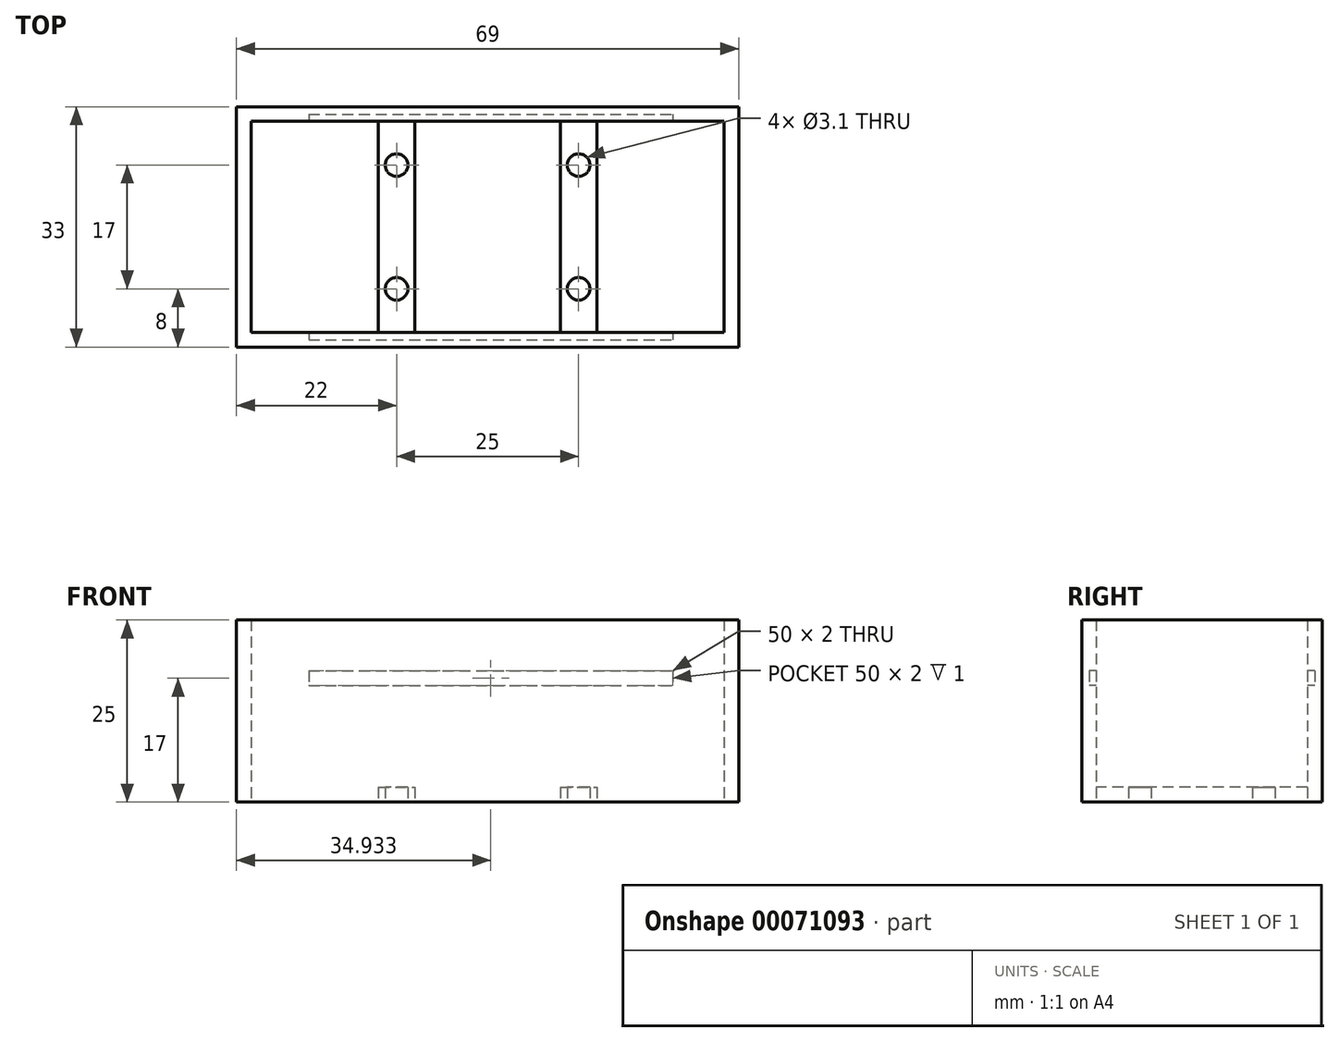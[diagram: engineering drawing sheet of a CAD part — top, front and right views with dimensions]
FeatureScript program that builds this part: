
annotation { "Feature Type Name" : "Feature", "Feature Type Description" : "" }
export const myFeature = defineFeature(function(context is Context, id is Id, definition is map)
    precondition{}
    {
        {
            var Q0;
            Q0=qCreatedBy(makeId("Top.planeOp"),FACE);
            var sketch = newSketch(context, id + "F0", { "sketchPlane" : qUnion([Q0])});
            skLineSegment(sketch, "E0.bottom", {"start": v(0, 0) * mm, "end": v(65, 0) * mm});
            skLineSegment(sketch, "E0.top", {"start": v(0, -29) * mm, "end": v(65, -29) * mm});
            skLineSegment(sketch, "E0.left", {"start": v(0, 0) * mm, "end": v(0, -29) * mm});
            skLineSegment(sketch, "E0.right", {"start": v(65, 0) * mm, "end": v(65, -29) * mm});
            skLineSegment(sketch, "E1.bottom", {"start": v(-2, 2) * mm, "end": v(67, 2) * mm});
            skLineSegment(sketch, "E1.top", {"start": v(-2, -31) * mm, "end": v(67, -31) * mm});
            skLineSegment(sketch, "E1.left", {"start": v(-2, 2) * mm, "end": v(-2, -31) * mm});
            skLineSegment(sketch, "E1.right", {"start": v(67, 2) * mm, "end": v(67, -31) * mm});
            skLineSegment(sketch, "E2.bottom", {"start": v(0, -29) * mm, "end": v(5, -29) * mm});
            skLineSegment(sketch, "E2.top", {"start": v(0, -24) * mm, "end": v(5, -24) * mm});
            skLineSegment(sketch, "E2.left", {"start": v(0, -29) * mm, "end": v(0, -24) * mm});
            skLineSegment(sketch, "E2.right", {"start": v(5, -29) * mm, "end": v(5, -24) * mm});
            skLineSegment(sketch, "E3.bottom", {"start": v(0, 0) * mm, "end": v(5, 0) * mm});
            skLineSegment(sketch, "E3.top", {"start": v(0, -5) * mm, "end": v(5, -5) * mm});
            skLineSegment(sketch, "E3.left", {"start": v(0, 0) * mm, "end": v(0, -5) * mm});
            skLineSegment(sketch, "E3.right", {"start": v(5, 0) * mm, "end": v(5, -5) * mm});
            skLineSegment(sketch, "E4.bottom", {"start": v(65, 0) * mm, "end": v(60, 0) * mm});
            skLineSegment(sketch, "E4.top", {"start": v(65, -5) * mm, "end": v(60, -5) * mm});
            skLineSegment(sketch, "E4.left", {"start": v(65, 0) * mm, "end": v(65, -5) * mm});
            skLineSegment(sketch, "E4.right", {"start": v(60, 0) * mm, "end": v(60, -5) * mm});
            skLineSegment(sketch, "E5.bottom", {"start": v(65, -29) * mm, "end": v(60, -29) * mm});
            skLineSegment(sketch, "E5.top", {"start": v(65, -24) * mm, "end": v(60, -24) * mm});
            skLineSegment(sketch, "E5.left", {"start": v(65, -29) * mm, "end": v(65, -24) * mm});
            skLineSegment(sketch, "E5.right", {"start": v(60, -29) * mm, "end": v(60, -24) * mm});
            skCircle(sketch, "E6", {"center": v(2.5, -2.5) * mm, "radius": 1.55 * mm});
            skCircle(sketch, "E7", {"center": v(2.5, -26.5) * mm, "radius": 1.55 * mm});
            skPoint(sketch, "E7.centerSnap0", {"position": v(2.5, -24) * mm});
            skPoint(sketch, "E7.centerSnap1", {"position": v(0, -26.5) * mm});
            skCircle(sketch, "E8", {"center": v(62.5, -26.5) * mm, "radius": 1.55 * mm});
            skPoint(sketch, "E8.centerSnap0", {"position": v(62.5, -24) * mm});
            skPoint(sketch, "E8.centerSnap1", {"position": v(5, -26.5) * mm});
            skCircle(sketch, "E9", {"center": v(62.5, -2.5) * mm, "radius": 1.55 * mm});
            skPoint(sketch, "E9.centerSnap0", {"position": v(60, -2.5) * mm});
            skPoint(sketch, "E9.centerSnap1", {"position": v(62.5, -5) * mm});
            skSolve(sketch);
        }
        {
            var Q0;
            Q0 = qSketchRegion(id + "F0", true);
            var Q1;
            Q1=makeQuery(id+"F0.imprint","IMPRINT",FACE,{"disambiguationData":[TD([[makeQuery(id+"F0.imprint","IMPRINT",EDGE,{"derivedFrom":sQuery(id+"F0.wireOp",EDGE,"E3.bottom")}),-1.0]])]});
            var Q2;
            Q2=makeQuery(id+"F0.imprint","IMPRINT",FACE,{"disambiguationData":[TD([[makeQuery(id+"F0.imprint","IMPRINT",EDGE,{"derivedFrom":sQuery(id+"F0.wireOp",EDGE,"E4.bottom")}),1.0]])]});
            var Q3;
            Q3=makeQuery(id+"F0.imprint","IMPRINT",FACE,{"disambiguationData":[TD([[makeQuery(id+"F0.imprint","IMPRINT",EDGE,{"derivedFrom":sQuery(id+"F0.wireOp",EDGE,"E5.bottom")}),-1.0]])]});
            var Q4;
            Q4=makeQuery(id+"F0.imprint","IMPRINT",FACE,{"disambiguationData":[TD([[makeQuery(id+"F0.imprint","IMPRINT",EDGE,{"derivedFrom":sQuery(id+"F0.wireOp",EDGE,"E2.bottom")}),1.0]])]});
            extrude(context, id + "F1", {"entities" : qUnion([Q0, Q1, Q2, Q3, Q4]), "depth" : 25 * mm});
        }
        {
            var Q0;
            Q0=makeQuery(id+"F1.opExtrude","CAP_FACE",FACE,{"disambiguationData":[OSD([sQuery(id+"F0.wireOp",EDGE,"E0.bottom"),sQuery(id+"F0.wireOp",EDGE,"E0.top"),sQuery(id+"F0.wireOp",EDGE,"E0.left"),sQuery(id+"F0.wireOp",EDGE,"E0.right"),sQuery(id+"F0.wireOp",EDGE,"E1.bottom"),sQuery(id+"F0.wireOp",EDGE,"E1.top"),sQuery(id+"F0.wireOp",EDGE,"E1.left"),sQuery(id+"F0.wireOp",EDGE,"E1.right"),sQuery(id+"F0.wireOp",EDGE,"E2.top"),sQuery(id+"F0.wireOp",EDGE,"E2.right"),sQuery(id+"F0.wireOp",EDGE,"E3.top"),sQuery(id+"F0.wireOp",EDGE,"E3.right"),sQuery(id+"F0.wireOp",EDGE,"E4.top"),sQuery(id+"F0.wireOp",EDGE,"E4.right"),sQuery(id+"F0.wireOp",EDGE,"E5.top"),sQuery(id+"F0.wireOp",EDGE,"E5.right"),sQuery(id+"F0.wireOp",EDGE,"E6"),sQuery(id+"F0.wireOp",EDGE,"E7"),sQuery(id+"F0.wireOp",EDGE,"E8"),sQuery(id+"F0.wireOp",EDGE,"E9")])],"isStart":false});
            cPlane(context, id + "F2", {"entities" : qUnion([Q0]), "cplaneType" : CPlaneType.OFFSET, "offset" : 9 * mm, "oppositeDirection" : true, "width" : 150 * mm, "height" : 150 * mm});
        }
        {
            var Q0;
            Q0=qCreatedBy(id+"F2.planeOp",FACE);
            var sketch = newSketch(context, id + "F3", { "sketchPlane" : qUnion([Q0])});
            skLineSegment(sketch, "E10.bottom", {"start": v(7.93, 1) * mm, "end": v(57.93, 1) * mm});
            skLineSegment(sketch, "E10.top", {"start": v(7.93, -30) * mm, "end": v(57.93, -30) * mm});
            skLineSegment(sketch, "E10.left", {"start": v(7.93, 1) * mm, "end": v(7.93, -30) * mm});
            skLineSegment(sketch, "E10.right", {"start": v(57.93, 1) * mm, "end": v(57.93, -30) * mm});
            skSolve(sketch);
        }
        {
            var Q0;
            Q0 = qSketchRegion(id + "F3", true);
            extrude(context, id + "F4", {"entities" : qUnion([Q0]), "operationType" : NewBodyOperationType.REMOVE, "depth" : 2 * mm});
        }
        {
            var Q0;
            Q0=makeQuery(id+"F1.opExtrude","CAP_FACE",FACE,{"disambiguationData":[OSD([sQuery(id+"F0.wireOp",EDGE,"E0.bottom"),sQuery(id+"F0.wireOp",EDGE,"E0.top"),sQuery(id+"F0.wireOp",EDGE,"E0.left"),sQuery(id+"F0.wireOp",EDGE,"E0.right"),sQuery(id+"F0.wireOp",EDGE,"E1.bottom"),sQuery(id+"F0.wireOp",EDGE,"E1.top"),sQuery(id+"F0.wireOp",EDGE,"E1.left"),sQuery(id+"F0.wireOp",EDGE,"E1.right"),sQuery(id+"F0.wireOp",EDGE,"E2.top"),sQuery(id+"F0.wireOp",EDGE,"E2.right"),sQuery(id+"F0.wireOp",EDGE,"E3.top"),sQuery(id+"F0.wireOp",EDGE,"E3.right"),sQuery(id+"F0.wireOp",EDGE,"E4.top"),sQuery(id+"F0.wireOp",EDGE,"E4.right"),sQuery(id+"F0.wireOp",EDGE,"E5.top"),sQuery(id+"F0.wireOp",EDGE,"E5.right"),sQuery(id+"F0.wireOp",EDGE,"E6"),sQuery(id+"F0.wireOp",EDGE,"E7"),sQuery(id+"F0.wireOp",EDGE,"E8"),sQuery(id+"F0.wireOp",EDGE,"E9")])],"isStart":false});
            cPlane(context, id + "F5", {"entities" : qUnion([Q0]), "cplaneType" : CPlaneType.OFFSET, "offset" : 6 * mm, "oppositeDirection" : true, "width" : 150 * mm, "height" : 150 * mm});
        }
        {
            var Q0;
            Q0=qCreatedBy(id+"F5.planeOp",FACE);
            var sketch = newSketch(context, id + "F6", { "sketchPlane" : qUnion([Q0])});
            skLineSegment(sketch, "E11.bottom", {"start": v(15.31, 0) * mm, "end": v(0, 0) * mm});
            skLineSegment(sketch, "E11.top", {"start": v(15.31, -28.57) * mm, "end": v(0, -28.57) * mm});
            skLineSegment(sketch, "E11.left", {"start": v(15.31, 0) * mm, "end": v(15.31, -28.57) * mm});
            skLineSegment(sketch, "E11.right", {"start": v(0, 0) * mm, "end": v(0, -28.57) * mm});
            skSolve(sketch);
        }
        {
            var Q0;
            Q0=makeQuery(id+"F6.imprint","IMPRINT",FACE,{"disambiguationData":[TD([[makeQuery(id+"F6.imprint","IMPRINT",EDGE,{"derivedFrom":sQuery(id+"F6.wireOp",EDGE,"E11.bottom")}),1.0]])]});
            extrude(context, id + "F7", {"entities" : qUnion([Q0]), "operationType" : NewBodyOperationType.REMOVE, "depth" : 2 * mm});
        }
        {
            var Q0;
            Q0=qCreatedBy(makeId("Top.planeOp"),FACE);
            var sketch = newSketch(context, id + "F8", { "sketchPlane" : qUnion([Q0])});
            skLineSegment(sketch, "E12.bottom", {"start": v(17.5, 0) * mm, "end": v(22.5, 0) * mm});
            skLineSegment(sketch, "E12.top", {"start": v(17.5, -29.94) * mm, "end": v(22.5, -29.94) * mm});
            skLineSegment(sketch, "E12.left", {"start": v(17.5, 0) * mm, "end": v(17.5, -29.94) * mm});
            skLineSegment(sketch, "E12.right", {"start": v(22.5, 0) * mm, "end": v(22.5, -29.94) * mm});
            skLineSegment(sketch, "E13.bottom", {"start": v(42.5, 0) * mm, "end": v(47.5, 0) * mm});
            skLineSegment(sketch, "E13.top", {"start": v(42.5, -29.94) * mm, "end": v(47.5, -29.94) * mm});
            skLineSegment(sketch, "E13.left", {"start": v(42.5, 0) * mm, "end": v(42.5, -29.94) * mm});
            skLineSegment(sketch, "E13.right", {"start": v(47.5, 0) * mm, "end": v(47.5, -29.94) * mm});
            skLineSegment(sketch, "E14", {"start": v(-7.92, -6) * mm, "end": v(80.41, -6) * mm, "construction": true});
            skLineSegment(sketch, "E15", {"start": v(-8.55, -23) * mm, "end": v(79, -23) * mm, "construction": true});
            skLineSegment(sketch, "E16", {"start": v(0, -14.5) * mm, "end": v(-11.82, -14.5) * mm, "construction": true});
            skCircle(sketch, "E17", {"center": v(20, -6) * mm, "radius": 1.55 * mm});
            skCircle(sketch, "E18", {"center": v(20, -23) * mm, "radius": 1.55 * mm});
            skCircle(sketch, "E19", {"center": v(45, -6) * mm, "radius": 1.55 * mm});
            skCircle(sketch, "E20", {"center": v(45, -23) * mm, "radius": 1.55 * mm});
            skSolve(sketch);
        }
        {
            var Q0;
            Q0 = qSketchRegion(id + "F8", true);
            extrude(context, id + "F9", {"entities" : qUnion([Q0]), "operationType" : NewBodyOperationType.ADD, "depth" : 2 * mm});
        }
    });
